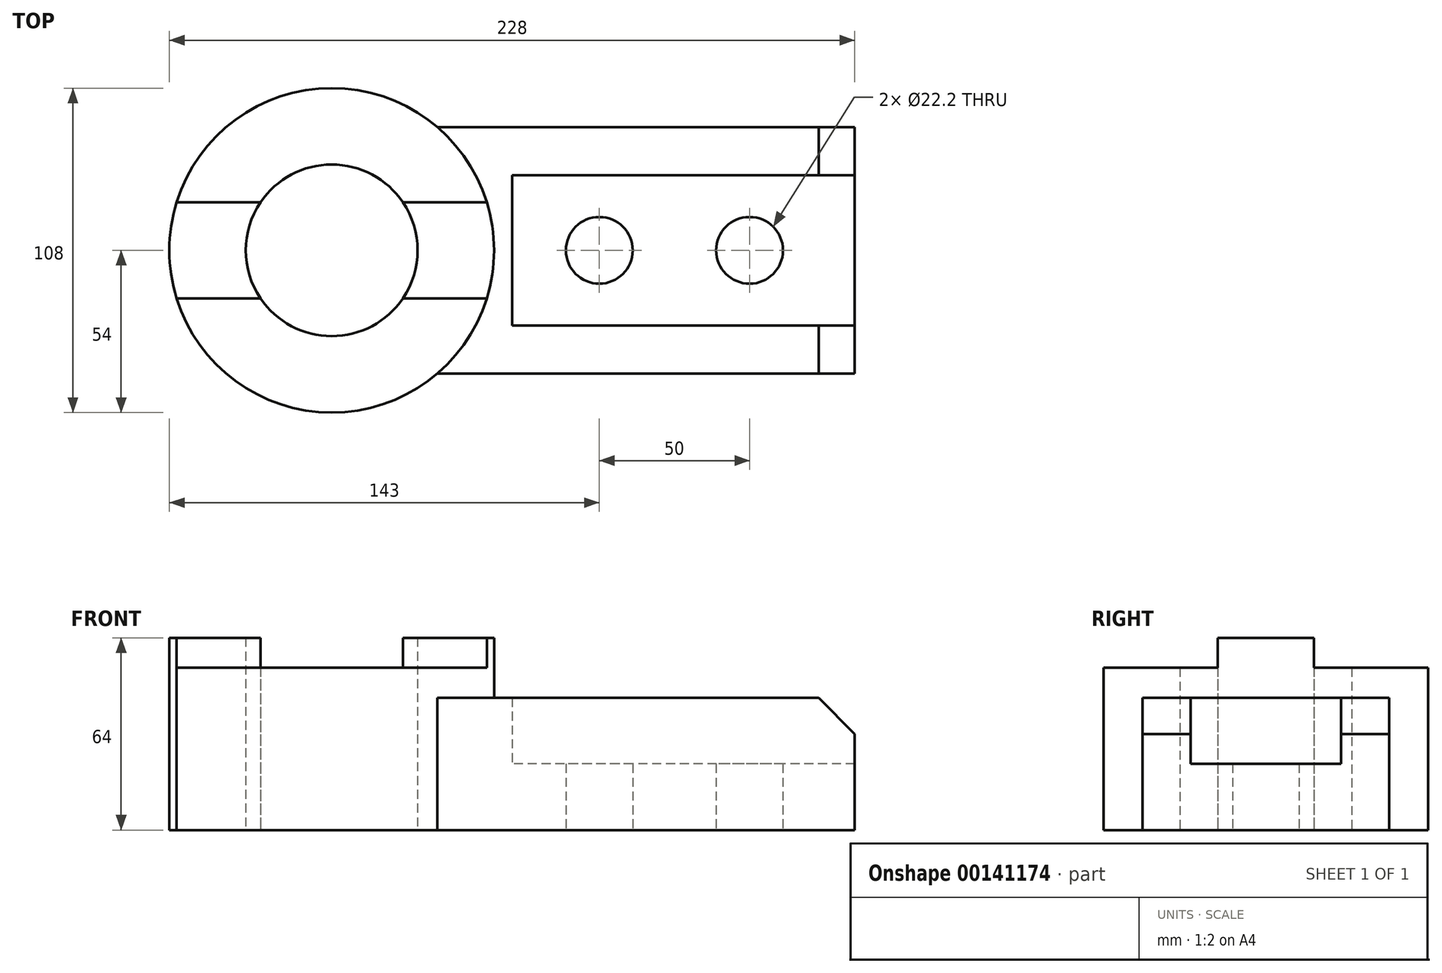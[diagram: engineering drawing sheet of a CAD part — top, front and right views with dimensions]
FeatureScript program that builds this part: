
annotation { "Feature Type Name" : "Feature", "Feature Type Description" : "" }
export const myFeature = defineFeature(function(context is Context, id is Id, definition is map)
    precondition{}
    {
        {
            var Q0;
            Q0=qCreatedBy(makeId("Top.planeOp"),FACE);
            var sketch = newSketch(context, id + "F0", { "sketchPlane" : qUnion([Q0])});
            skCircle(sketch, "E0", {"center": v(0, 0) * mm, "radius": 54 * mm});
            skLineSegment(sketch, "E1", {"start": v(35.14, 41) * mm, "end": v(174, 41) * mm});
            skLineSegment(sketch, "E2", {"start": v(174, 41) * mm, "end": v(174, -41) * mm});
            skLineSegment(sketch, "E3", {"start": v(174, -41) * mm, "end": v(35.14, -41) * mm});
            skLineSegment(sketch, "E4", {"start": v(174, -25) * mm, "end": v(60, -25) * mm});
            skLineSegment(sketch, "E5", {"start": v(60, -25) * mm, "end": v(60, 25) * mm});
            skLineSegment(sketch, "E6", {"start": v(60, 25) * mm, "end": v(174, 25) * mm});
            skCircle(sketch, "E7", {"center": v(89, 0) * mm, "radius": 11.1 * mm});
            skCircle(sketch, "E8", {"center": v(139, 0) * mm, "radius": 11.1 * mm});
            skLineSegment(sketch, "E9", {"start": v(35.14, 41) * mm, "end": v(35.14, -41) * mm, "construction": true});
            skCircle(sketch, "E10", {"center": v(0, 0) * mm, "radius": 28.57 * mm});
            skLineSegment(sketch, "E11.bottom", {"start": v(51.58, 16) * mm, "end": v(23.68, 16) * mm});
            skLineSegment(sketch, "E11.top", {"start": v(51.58, -16) * mm, "end": v(23.68, -16) * mm});
            skLineSegment(sketch, "E12.trimOffspring", {"start": v(-23.68, 16) * mm, "end": v(-51.58, 16) * mm});
            skLineSegment(sketch, "E13.trimOffspring", {"start": v(-23.68, -16) * mm, "end": v(-51.58, -16) * mm});
            skSolve(sketch);
        }
        {
            var Q0;
            {var subQ0=sQuery(id+"F0.wireOp",EDGE,"E11.bottom");Q0=makeQuery(id+"F0.imprint","IMPRINT",FACE,{"disambiguationData":[TD([[makeQuery(id+"F0.imprint","IMPRINT",EDGE,{"derivedFrom":subQ0}),-1.0]])]});}
            var Q1;
            {var subQ0=sQuery(id+"F0.wireOp",EDGE,"E11.top");Q1=makeQuery(id+"F0.imprint","IMPRINT",FACE,{"disambiguationData":[TD([[makeQuery(id+"F0.imprint","IMPRINT",EDGE,{"derivedFrom":subQ0}),1.0]])]});}
            extrude(context, id + "F1", {"entities" : qUnion([Q0, Q1]), "depth" : 54 * mm});
        }
        {
            var Q0;
            {var subQ0=sQuery(id+"F0.wireOp",EDGE,"E12.trimOffspring");Q0=makeQuery(id+"F0.imprint","IMPRINT",FACE,{"disambiguationData":[TD([[makeQuery(id+"F0.imprint","IMPRINT",EDGE,{"derivedFrom":subQ0}),1.0]])]});}
            var Q1;
            {var subQ0=sQuery(id+"F0.wireOp",EDGE,"E11.bottom");Q1=makeQuery(id+"F0.imprint","IMPRINT",FACE,{"disambiguationData":[TD([[makeQuery(id+"F0.imprint","IMPRINT",EDGE,{"derivedFrom":subQ0}),1.0]])]});}
            extrude(context, id + "F2", {"entities" : qUnion([Q0, Q1]), "depth" : 64 * mm});
        }
        {
            var Q0;
            {var subQ0=sQuery(id+"F0.wireOp",EDGE,"E1");Q0=makeQuery(id+"F0.imprint","IMPRINT",FACE,{"disambiguationData":[TD([[makeQuery(id+"F0.imprint","IMPRINT",EDGE,{"derivedFrom":subQ0}),-1.0]])]});}
            extrude(context, id + "F3", {"entities" : qUnion([Q0]), "operationType" : NewBodyOperationType.ADD, "depth" : 44 * mm});
        }
        {
            var Q0;
            {var subQ1=sQuery(id+"F0.wireOp",EDGE,"E4");Q0=makeQuery(id+"F0.imprint","IMPRINT",FACE,{"disambiguationData":[TD([[makeQuery(id+"F0.imprint","IMPRINT",EDGE,{"derivedFrom":subQ1}),-1.0]])]});}
            extrude(context, id + "F4", {"entities" : qUnion([Q0]), "operationType" : NewBodyOperationType.ADD, "depth" : 22 * mm});
        }
        {
            var Q0;
            {var subQ0=sQuery(id+"F0.wireOp",EDGE,"E2");Q0=makeQuery(id+"F3.opExtrude","CAP_EDGE",EDGE,{"disambiguationData":[OSD([subQ0]),TDD([makeQuery(id+"F0.imprint","IMPRINT",EDGE,{"disambiguationData":[TD([[makeQuery(id+"F0.imprint","INTERSECT",VERTEX,{"derivedFrom":[subQ0,sQuery(id+"F0.wireOp",EDGE,"E3")]}),1.0]])],"derivedFrom":subQ0})])],"isStart":false});}
            var Q1;
            {var subQ0=sQuery(id+"F0.wireOp",EDGE,"E2");Q1=makeQuery(id+"F3.opExtrude","CAP_EDGE",EDGE,{"disambiguationData":[OSD([subQ0]),TDD([makeQuery(id+"F0.imprint","IMPRINT",EDGE,{"disambiguationData":[TD([[makeQuery(id+"F0.imprint","INTERSECT",VERTEX,{"derivedFrom":[sQuery(id+"F0.wireOp",EDGE,"E1"),subQ0]}),-1.0]])],"derivedFrom":subQ0})])],"isStart":false});}
            chamfer(context, id + "F5", {"entities" : qUnion([Q0, Q1]), "chamferType" : ChamferType.OFFSET_ANGLE, "width" : 12 * mm, "oppositeDirection" : false, "angle" : 45 * degree, "tangentPropagation" : true});
        }
    });
